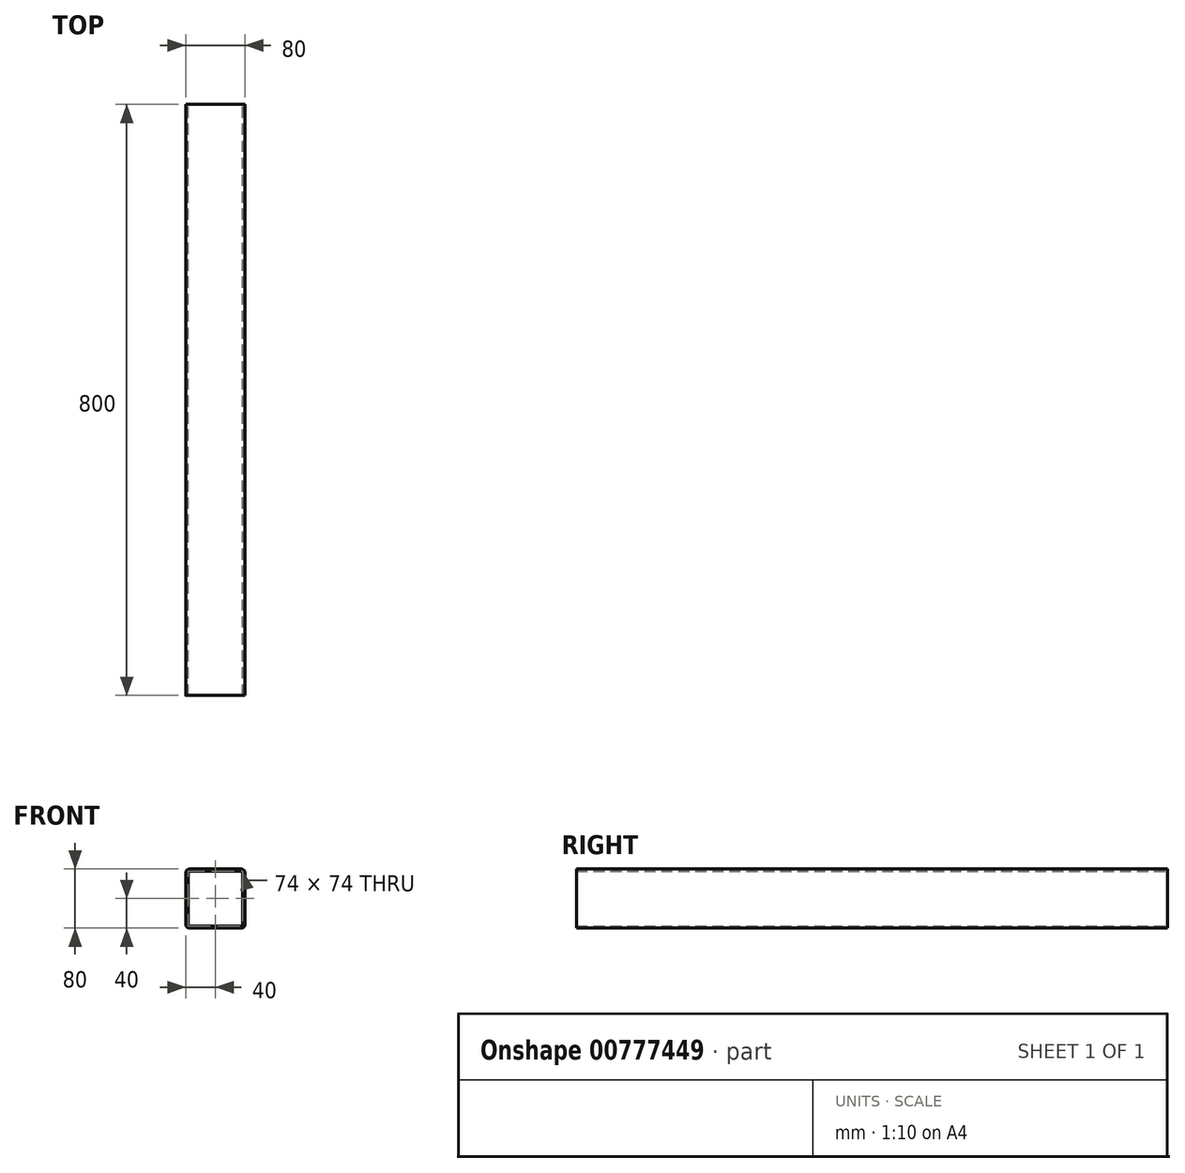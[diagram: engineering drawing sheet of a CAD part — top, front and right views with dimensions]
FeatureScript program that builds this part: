
annotation { "Feature Type Name" : "Feature", "Feature Type Description" : "" }
export const myFeature = defineFeature(function(context is Context, id is Id, definition is map)
    precondition{}
    {
        {
            var Q0;
            Q0=qCreatedBy(makeId("Front.planeOp"),FACE);
            var sketch = newSketch(context, id + "F0", { "sketchPlane" : qUnion([Q0])});
            skLineSegment(sketch, "E0.bottom", {"start": v(40, -40) * mm, "end": v(-40, -40) * mm});
            skLineSegment(sketch, "E0.top", {"start": v(40, 40) * mm, "end": v(-40, 40) * mm});
            skLineSegment(sketch, "E0.left", {"start": v(40, -40) * mm, "end": v(40, 40) * mm});
            skLineSegment(sketch, "E0.right", {"start": v(-40, -40) * mm, "end": v(-40, 40) * mm});
            skPoint(sketch, "E0.middle", {"position": v(0, 0) * mm});
            skLineSegment(sketch, "E1.0", {"start": v(37, 37) * mm, "end": v(-37, 37) * mm});
            skLineSegment(sketch, "E1.1", {"start": v(37, -37) * mm, "end": v(37, 37) * mm});
            skLineSegment(sketch, "E1.2", {"start": v(37, -37) * mm, "end": v(-37, -37) * mm});
            skLineSegment(sketch, "E1.3", {"start": v(-37, -37) * mm, "end": v(-37, 37) * mm});
            skSolve(sketch);
        }
        {
            var Q0;
            Q0 = qSketchRegion(id + "F0", true);
            extrude(context, id + "F1", {"entities" : qUnion([Q0]), "depth" : 800 * mm, "offsetDistance" : 25 * mm});
        }
        {
            var Q0;
            Q0=makeQuery(id+"F1.opExtrude","SWEPT_EDGE",EDGE,{"disambiguationData":[OSD([sQuery(id+"F0.wireOp",EDGE,"E0.top"),sQuery(id+"F0.wireOp",EDGE,"E0.left")])]});
            var Q1;
            Q1=makeQuery(id+"F1.opExtrude","SWEPT_EDGE",EDGE,{"disambiguationData":[OSD([sQuery(id+"F0.wireOp",EDGE,"E0.top"),sQuery(id+"F0.wireOp",EDGE,"E0.right")])]});
            var Q2;
            Q2=makeQuery(id+"F1.opExtrude","SWEPT_EDGE",EDGE,{"disambiguationData":[OSD([sQuery(id+"F0.wireOp",EDGE,"E0.bottom"),sQuery(id+"F0.wireOp",EDGE,"E0.left")])]});
            var Q3;
            Q3=makeQuery(id+"F1.opExtrude","SWEPT_EDGE",EDGE,{"disambiguationData":[OSD([sQuery(id+"F0.wireOp",EDGE,"E0.bottom"),sQuery(id+"F0.wireOp",EDGE,"E0.right")])]});
            fillet(context, id + "F2", {"entities" : qUnion([Q0, Q1, Q2, Q3]), "radius" : 5 * mm, "tangentPropagation" : true, "allowEdgeOverflow" : false});
        }
    });
